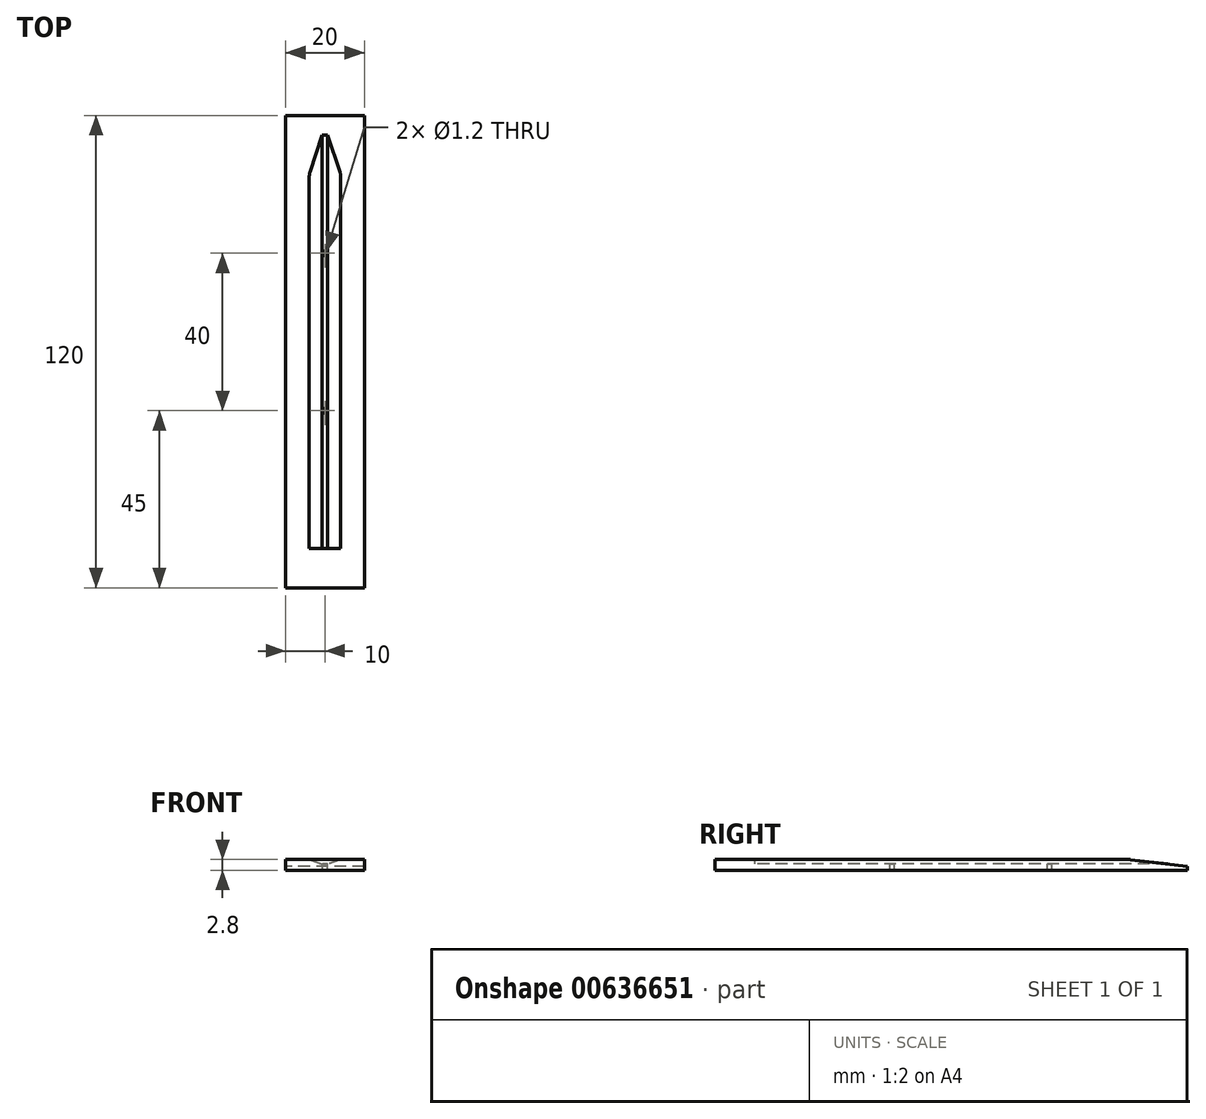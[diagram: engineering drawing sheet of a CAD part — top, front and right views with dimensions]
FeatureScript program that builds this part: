
annotation { "Feature Type Name" : "Feature", "Feature Type Description" : "" }
export const myFeature = defineFeature(function(context is Context, id is Id, definition is map)
    precondition{}
    {
        {
            var Q0;
            Q0=qCreatedBy(makeId("Right.planeOp"),FACE);
            var sketch = newSketch(context, id + "F0", { "sketchPlane" : qUnion([Q0])});
            skLineSegment(sketch, "E0", {"start": v(0, 0) * mm, "end": v(120, 0) * mm});
            skLineSegment(sketch, "E1", {"start": v(120, 0) * mm, "end": v(120, 1) * mm});
            skLineSegment(sketch, "E2", {"start": v(120, 1) * mm, "end": v(105, 2.8) * mm});
            skLineSegment(sketch, "E3", {"start": v(105, 2.8) * mm, "end": v(0, 2.8) * mm});
            skLineSegment(sketch, "E4", {"start": v(0, 2.8) * mm, "end": v(0, 0) * mm});
            skSolve(sketch);
        }
        {
            var Q0;
            Q0 = qSketchRegion(id + "F0", true);
            extrude(context, id + "F1", {"entities" : qUnion([Q0]), "depth" : 20 * mm, "offsetDistance" : 25 * mm});
        }
        {
            var Q0;
            Q0=makeQuery(id+"F1.opExtrude","SWEPT_FACE",FACE,{"disambiguationData":[OSD([sQuery(id+"F0.wireOp",EDGE,"E4")])]});
            var sketch = newSketch(context, id + "F2", { "sketchPlane" : qUnion([Q0])});
            skLineSegment(sketch, "E5", {"start": v(6, 1.6) * mm, "end": v(14, 1.6) * mm});
            skLineSegment(sketch, "E6", {"start": v(10, 1.6) * mm, "end": v(10, 2.8) * mm, "construction": true});
            skLineSegment(sketch, "E7", {"start": v(6, 1.6) * mm, "end": v(6, 2.8) * mm});
            skLineSegment(sketch, "E8", {"start": v(14, 1.6) * mm, "end": v(14, 2.8) * mm});
            skLineSegment(sketch, "E9", {"start": v(6, 2.8) * mm, "end": v(9.3, 1.6) * mm});
            skLineSegment(sketch, "E10.MirrorCS", {"start": v(14, 2.8) * mm, "end": v(10.7, 1.6) * mm});
            skSolve(sketch);
        }
        {
            var Q0;
            {var subQ0=sQuery(id+"F2.wireOp",EDGE,"E9");Q0=makeQuery(id+"F2.imprint","IMPRINT",FACE,{"disambiguationData":[TD([[makeQuery(id+"F2.imprint","IMPRINT",EDGE,{"derivedFrom":subQ0}),1.0]])]});}
            var Q1;
            Q1=makeQuery(id+"F1.opExtrude","SWEPT_FACE",FACE,{"disambiguationData":[OSD([sQuery(id+"F0.wireOp",EDGE,"E1")])]});
            extrude(context, id + "F3", {"entities" : qUnion([Q0]), "oppositeDirection" : true, "depth" : 120 * mm, "endBoundEntityFace" : qUnion([Q1]), "offsetDistance" : 25 * mm});
        }
        {
            var Q0;
            Q0=makeQuery(id+"F3.opExtrude","SWEPT_BODY",BODY,{"disambiguationData":[OSD([sQuery(id+"F0.wireOp",EDGE,"E3"),sQuery(id+"F0.wireOp",EDGE,"E4"),sQuery(id+"F2.wireOp",EDGE,"E5"),sQuery(id+"F2.wireOp",EDGE,"E7"),sQuery(id+"F2.wireOp",EDGE,"E8")])]});
            transform(context, id + "F4", {"entities" : qUnion([Q0]), "transformType" : TransformType.TRANSLATION_3D, "dx" : 0 * mm, "dy" : 10 * mm, "dz" : 0 * mm, "makeCopy" : false});
        }
        {
            var Q0;
            Q0=makeQuery(id+"F3.opExtrude","SWEPT_BODY",BODY,{"disambiguationData":[OSD([sQuery(id+"F0.wireOp",EDGE,"E3"),sQuery(id+"F0.wireOp",EDGE,"E4"),sQuery(id+"F2.wireOp",EDGE,"E5"),sQuery(id+"F2.wireOp",EDGE,"E7"),sQuery(id+"F2.wireOp",EDGE,"E8")])]});
            var Q1;
            Q1=makeQuery(id+"F1.opExtrude","SWEPT_BODY",BODY,{"disambiguationData":[OSD([sQuery(id+"F0.wireOp",EDGE,"E0"),sQuery(id+"F0.wireOp",EDGE,"E1"),sQuery(id+"F0.wireOp",EDGE,"E2"),sQuery(id+"F0.wireOp",EDGE,"E3"),sQuery(id+"F0.wireOp",EDGE,"E4")])]});
            booleanBodies(context, id + "F5", {"operationType" : BooleanOperationType.SUBTRACTION, "tools" : qUnion([Q0]), "targets" : qUnion([Q1])});
        }
        {
            var Q0;
            Q0=makeQuery(id+"F5.opBoolean","COPY",FACE,{"derivedFrom":makeQuery(id+"F3.opExtrude","SWEPT_FACE",FACE,{"disambiguationData":[OSD([sQuery(id+"F2.wireOp",EDGE,"E5")])]})});
            var sketch = newSketch(context, id + "F6", { "sketchPlane" : qUnion([Q0])});
            skCircle(sketch, "E11", {"center": v(10, 85) * mm, "radius": 0.6 * mm});
            skPoint(sketch, "E11.centerSnap0", {"position": v(10, 115) * mm});
            skCircle(sketch, "E12", {"center": v(10, 45) * mm, "radius": 0.6 * mm});
            skSolve(sketch);
        }
        {
            var Q0;
            Q0 = qSketchRegion(id + "F6", true);
            extrude(context, id + "F7", {"entities" : qUnion([Q0]), "operationType" : NewBodyOperationType.REMOVE, "oppositeDirection" : true, "depth" : 25 * mm, "offsetDistance" : 25 * mm});
        }
        {
            var Q0;
            {var subQ0=sQuery(id+"F0.wireOp",EDGE,"E3");var subQ1=sQuery(id+"F0.wireOp",EDGE,"E2");Q0=makeQuery(id+"F5.opBoolean","SPLIT",EDGE,{"disambiguationData":[TD([makeQuery(id+"F3.opExtrude","SWEPT_FACE",FACE,{"disambiguationData":[OSD([sQuery(id+"F2.wireOp",EDGE,"E10.MirrorCS")])]})])],"derivedFrom":makeQuery(id+"F1.opExtrude","SWEPT_EDGE",EDGE,{"disambiguationData":[OSD([subQ1,subQ0])]})});}
            var Q1;
            {var subQ0=sQuery(id+"F0.wireOp",EDGE,"E3");var subQ1=sQuery(id+"F0.wireOp",EDGE,"E2");Q1=makeQuery(id+"F5.opBoolean","SPLIT",EDGE,{"disambiguationData":[TD([makeQuery(id+"F3.opExtrude","SWEPT_FACE",FACE,{"disambiguationData":[OSD([sQuery(id+"F2.wireOp",EDGE,"E9")])]})])],"derivedFrom":makeQuery(id+"F1.opExtrude","SWEPT_EDGE",EDGE,{"disambiguationData":[OSD([subQ1,subQ0])]})});}
            fillet(context, id + "F8", {"entities" : qUnion([Q0, Q1]), "radius" : 10 * mm, "tangentPropagation" : true, "allowEdgeOverflow" : false});
        }
    });
